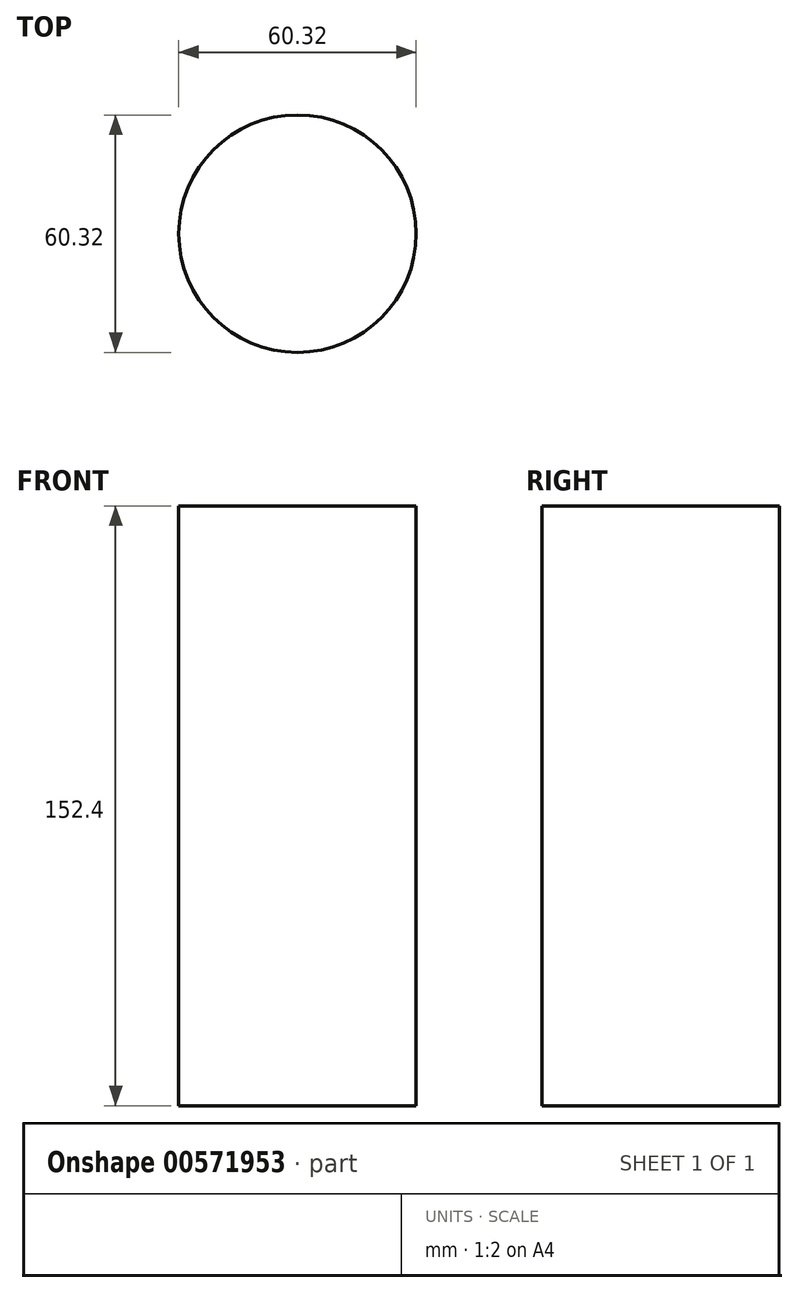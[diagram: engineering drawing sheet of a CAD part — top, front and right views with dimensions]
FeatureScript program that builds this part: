
annotation { "Feature Type Name" : "Feature", "Feature Type Description" : "" }
export const myFeature = defineFeature(function(context is Context, id is Id, definition is map)
    precondition{}
    {
        {
            var Q0;
            Q0=qCreatedBy(makeId("Top.planeOp"),FACE);
            var sketch = newSketch(context, id + "F0", { "sketchPlane" : qUnion([Q0])});
            skCircle(sketch, "E0", {"center": v(0, 0) * mm, "radius": 30.16 * mm});
            skSolve(sketch);
        }
        {
            var Q0;
            Q0=makeQuery(id+"F0.imprint","IMPRINT",FACE,{"disambiguationData":[TD([[makeQuery(id+"F0.imprint","IMPRINT",EDGE,{"derivedFrom":sQuery(id+"F0.wireOp",EDGE,"E0")}),1.0]])]});
            extrude(context, id + "F1", {"entities" : qUnion([Q0]), "depth" : 152.4 * mm, "offsetDistance" : 25.4 * mm});
        }
    });
